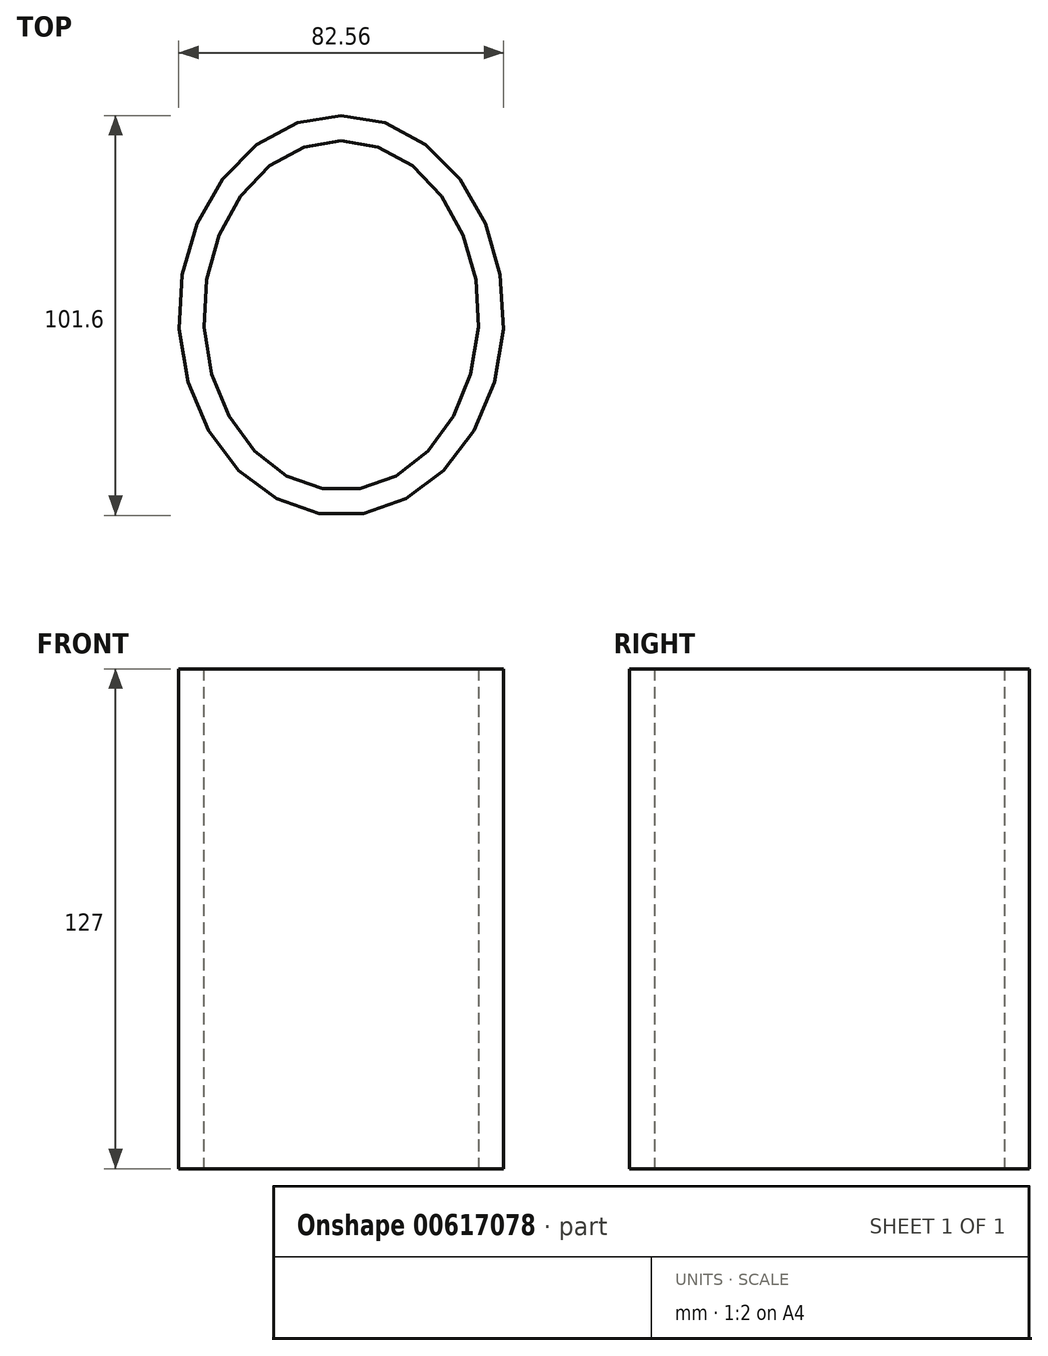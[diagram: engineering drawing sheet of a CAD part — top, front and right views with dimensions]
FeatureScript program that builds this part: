
annotation { "Feature Type Name" : "Feature", "Feature Type Description" : "" }
export const myFeature = defineFeature(function(context is Context, id is Id, definition is map)
    precondition{}
    {
        {
            var Q0;
            Q0=qCreatedBy(makeId("Top.planeOp"),FACE);
            var sketch = newSketch(context, id + "F0", { "sketchPlane" : qUnion([Q0])});
            skEllipse(sketch, "E0", {"center": v(0, 0) * mm, "majorRadius": 50.8 * mm, "minorRadius": 41.28 * mm, "majorAxis": v(0, 1)});
            skEllipse(sketch, "E1", {"center": v(0, 0) * mm, "majorRadius": 44.45 * mm, "minorRadius": 34.93 * mm, "majorAxis": v(0, 1)});
            skSolve(sketch);
        }
        {
            var Q0;
            Q0 = qSketchRegion(id + "F0", true);
            extrude(context, id + "F1", {"entities" : qUnion([Q0]), "depth" : 63.5 * mm, "offsetDistance" : 25.4 * mm, "hasSecondDirection" : true, "secondDirectionOppositeDirection" : true, "secondDirectionDepth" : 63.5 * mm});
        }
    });
